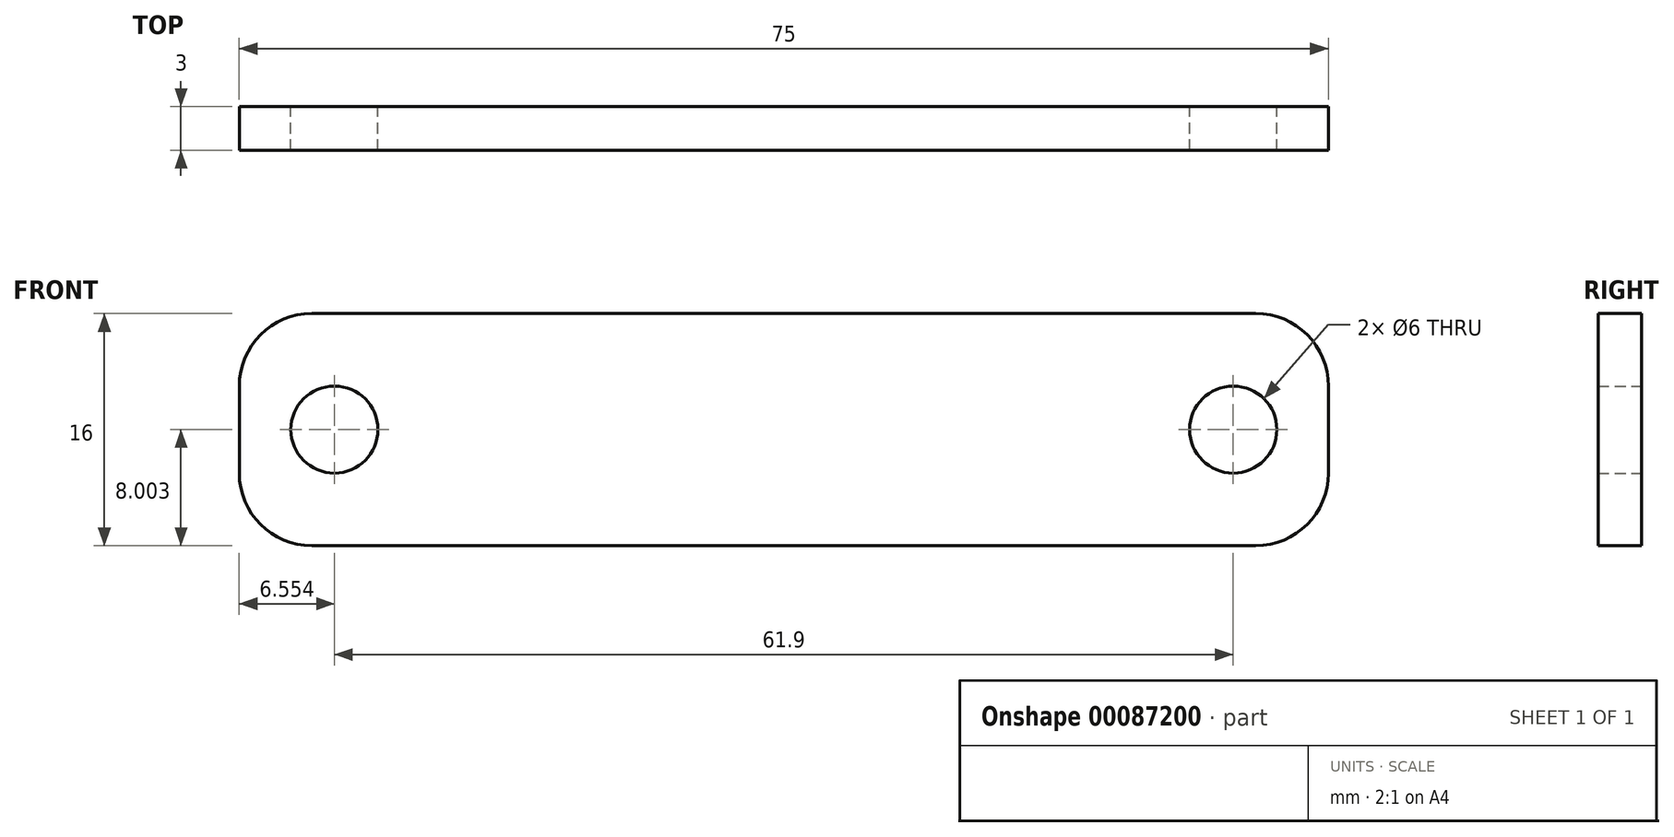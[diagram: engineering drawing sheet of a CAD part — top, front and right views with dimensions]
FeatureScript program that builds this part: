
annotation { "Feature Type Name" : "Feature", "Feature Type Description" : "" }
export const myFeature = defineFeature(function(context is Context, id is Id, definition is map)
    precondition{}
    {
        {
            var Q0;
            Q0=qCreatedBy(makeId("Front.planeOp"),FACE);
            var sketch = newSketch(context, id + "F0", { "sketchPlane" : qUnion([Q0])});
            skLineSegment(sketch, "E0", {"start": v(-178.89, 33.38) * mm, "end": v(-116.99, 33.38) * mm, "construction": true});
            skCircle(sketch, "E1", {"center": v(-178.89, 33.38) * mm, "radius": 3 * mm});
            skCircle(sketch, "E2", {"center": v(-116.99, 33.38) * mm, "radius": 3 * mm});
            skLineSegment(sketch, "E3.bottom", {"start": v(-115.44, 41.38) * mm, "end": v(-180.44, 41.38) * mm});
            skLineSegment(sketch, "E3.top", {"start": v(-115.44, 25.38) * mm, "end": v(-180.44, 25.38) * mm});
            skLineSegment(sketch, "E3.left", {"start": v(-110.44, 36.38) * mm, "end": v(-110.44, 30.38) * mm});
            skLineSegment(sketch, "E3.right", {"start": v(-185.44, 36.38) * mm, "end": v(-185.44, 30.38) * mm});
            skPoint(sketch, "E3.middle", {"position": v(-147.94, 33.38) * mm});
            skPoint(sketch, "E4.visualSharp", {"position": v(-110.44, 41.38) * mm});
            skArc(sketch, "E4.filletArc", {"start": v(-110.44, 36.38) * mm, "mid": v(-111.9, 39.92) * mm, "end": v(-115.44, 41.38) * mm});
            skPoint(sketch, "E5.visualSharp", {"position": v(-110.44, 25.38) * mm});
            skArc(sketch, "E5.filletArc", {"start": v(-115.44, 25.38) * mm, "mid": v(-111.9, 26.85) * mm, "end": v(-110.44, 30.38) * mm});
            skPoint(sketch, "E6.visualSharp", {"position": v(-185.44, 25.38) * mm});
            skArc(sketch, "E6.filletArc", {"start": v(-185.44, 30.38) * mm, "mid": v(-183.97, 26.85) * mm, "end": v(-180.44, 25.38) * mm});
            skPoint(sketch, "E7.visualSharp", {"position": v(-185.44, 41.38) * mm});
            skArc(sketch, "E7.filletArc", {"start": v(-180.44, 41.38) * mm, "mid": v(-183.97, 39.92) * mm, "end": v(-185.44, 36.38) * mm});
            skSolve(sketch);
        }
        {
            var Q0;
            Q0=qSketchRegion(id+"F0",true);
            extrude(context, id + "F1", {"entities" : qUnion([Q0]), "depth" : 3 * mm});
        }
    });
